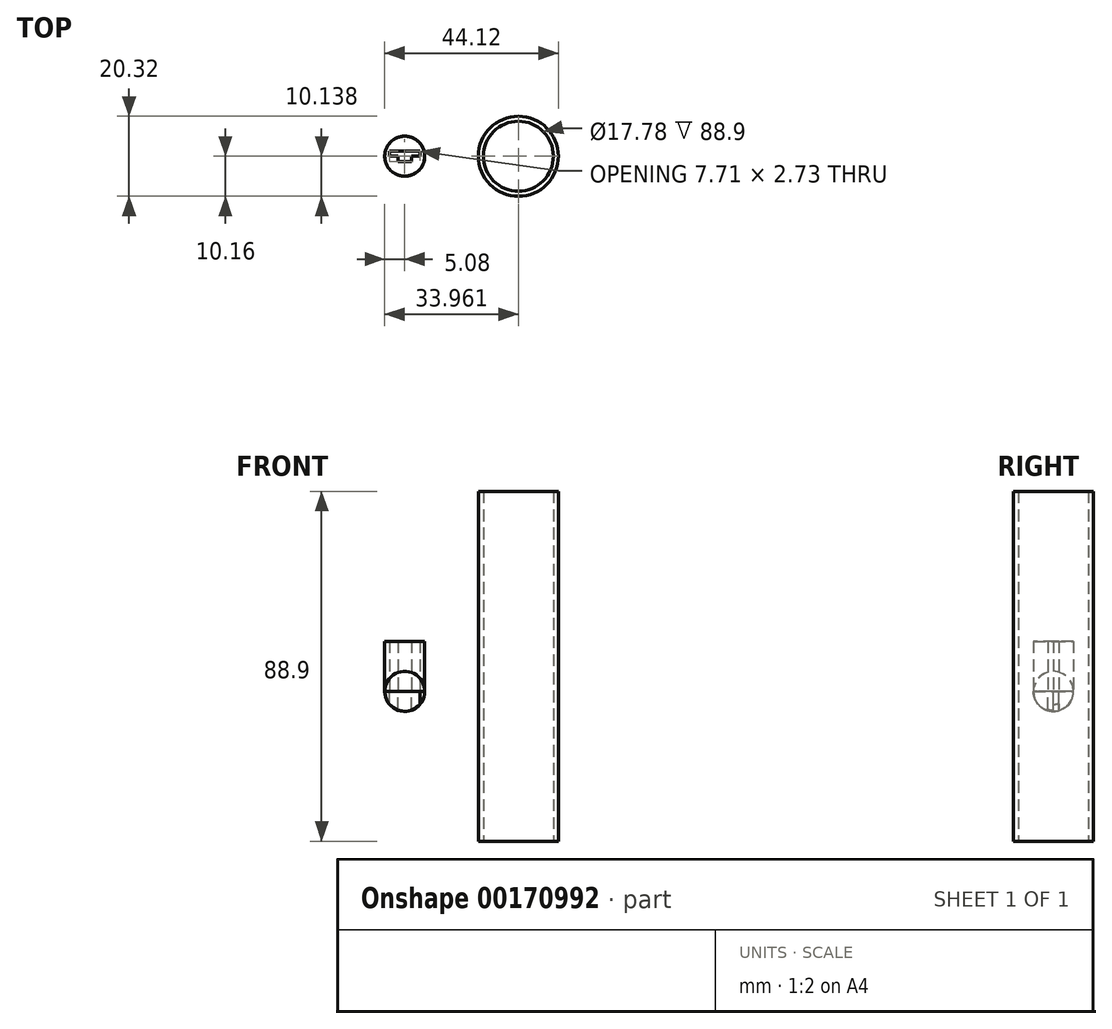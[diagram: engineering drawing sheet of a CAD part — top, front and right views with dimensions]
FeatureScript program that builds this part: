
annotation { "Feature Type Name" : "Feature", "Feature Type Description" : "" }
export const myFeature = defineFeature(function(context is Context, id is Id, definition is map)
    precondition{}
    {
        {
            var Q0;
            Q0=qCreatedBy(makeId("Top.planeOp"),FACE);
            var sketch = newSketch(context, id + "F0", { "sketchPlane" : qUnion([Q0])});
            skLineSegment(sketch, "E0", {"start": v(0, 1.35) * mm, "end": v(-3.86, 1.35) * mm});
            skLineSegment(sketch, "E1", {"start": v(-3.86, 0.01) * mm, "end": v(-1.71, 0.01) * mm});
            skLineSegment(sketch, "E2", {"start": v(-1.71, 0.01) * mm, "end": v(-1.71, -1.37) * mm});
            skLineSegment(sketch, "E3", {"start": v(-1.71, -1.37) * mm, "end": v(0, -1.37) * mm});
            skLineSegment(sketch, "E4", {"start": v(-3.86, 1.35) * mm, "end": v(-3.86, 0.01) * mm});
            skLineSegment(sketch, "E5.MirrorCS", {"start": v(1.71, 0.01) * mm, "end": v(1.71, -1.37) * mm});
            skLineSegment(sketch, "E6.MirrorCS", {"start": v(3.86, 1.35) * mm, "end": v(3.86, 0.01) * mm});
            skLineSegment(sketch, "E7.MirrorCS", {"start": v(3.86, 0.01) * mm, "end": v(1.71, 0.01) * mm});
            skLineSegment(sketch, "E8.MirrorCS", {"start": v(1.71, -1.37) * mm, "end": v(0, -1.37) * mm});
            skLineSegment(sketch, "E9.MirrorCS", {"start": v(0, 1.35) * mm, "end": v(3.86, 1.35) * mm});
            skCircle(sketch, "E10", {"center": v(0, 0) * mm, "radius": 5.08 * mm});
            skLineSegment(sketch, "E11", {"start": v(0, 0) * mm, "end": v(0, 1.35) * mm});
            skLineSegment(sketch, "E12", {"start": v(0, 0) * mm, "end": v(0, -1.37) * mm});
            skSolve(sketch);
        }
        {
            var Q0;
            Q0=makeQuery(id+"F0.imprint","IMPRINT",FACE,{"disambiguationData":[TD([[makeQuery(id+"F0.imprint","IMPRINT",EDGE,{"derivedFrom":sQuery(id+"F0.wireOp",EDGE,"E0")}),-1.0]])]});
            cPlane(context, id + "F1", {"entities" : qUnion([Q0]), "cplaneType" : CPlaneType.OFFSET, "offset" : 6.35 * mm, "width" : 152.4 * mm, "height" : 152.4 * mm});
        }
        {
            var Q0;
            Q0=makeQuery(id+"F0.imprint","IMPRINT",FACE,{"disambiguationData":[TD([[makeQuery(id+"F0.imprint","IMPRINT",EDGE,{"derivedFrom":sQuery(id+"F0.wireOp",EDGE,"E0")}),-1.0]])]});
            cPlane(context, id + "F2", {"entities" : qUnion([Q0]), "cplaneType" : CPlaneType.OFFSET, "offset" : 6.35 * mm, "oppositeDirection" : true, "width" : 152.4 * mm, "height" : 152.4 * mm});
        }
        {
            var Q0;
            Q0=qCreatedBy(id+"F1.planeOp",FACE);
            var sketch = newSketch(context, id + "F3", { "sketchPlane" : qUnion([Q0])});
            skArc(sketch, "E13", {"start": v(0, 5.08) * mm, "mid": v(-5.08, 0) * mm, "end": v(0, -5.08) * mm});
            skLineSegment(sketch, "E14", {"start": v(0, 0) * mm, "end": v(0, 1.34) * mm});
            skLineSegment(sketch, "E15", {"start": v(0, 1.34) * mm, "end": v(-3.86, 1.34) * mm});
            skLineSegment(sketch, "E16.MirrorCS", {"start": v(0, 1.34) * mm, "end": v(3.86, 1.34) * mm});
            skLineSegment(sketch, "E17", {"start": v(3.86, 1.34) * mm, "end": v(3.86, 0) * mm});
            skLineSegment(sketch, "E18", {"start": v(3.86, 0) * mm, "end": v(1.71, 0) * mm});
            skLineSegment(sketch, "E19", {"start": v(1.71, 0) * mm, "end": v(1.71, -1.39) * mm});
            skLineSegment(sketch, "E20", {"start": v(1.71, -1.39) * mm, "end": v(-1.71, -1.39) * mm});
            skLineSegment(sketch, "E21", {"start": v(-1.71, -1.39) * mm, "end": v(-1.71, 0) * mm});
            skLineSegment(sketch, "E22", {"start": v(-1.71, 0) * mm, "end": v(-3.86, 0) * mm});
            skLineSegment(sketch, "E23", {"start": v(-3.86, 0) * mm, "end": v(-3.86, 1.34) * mm});
            skLineSegment(sketch, "E24", {"start": v(-6.66, 0) * mm, "end": v(7.05, 0) * mm, "construction": true});
            skLineSegment(sketch, "E25", {"start": v(0, 5.08) * mm, "end": v(0, -5.08) * mm});
            skPoint(sketch, "E25.endSnap0", {"position": v(0, -1.39) * mm});
            skSolve(sketch);
        }
        {
            var Q0;
            Q0=qCreatedBy(id+"F2.planeOp",FACE);
            var sketch = newSketch(context, id + "F4", { "sketchPlane" : qUnion([Q0])});
            skArc(sketch, "E26", {"start": v(0, 5.08) * mm, "mid": v(-5.08, 0) * mm, "end": v(0, -5.08) * mm});
            skLineSegment(sketch, "E27", {"start": v(0, 0) * mm, "end": v(0, 1.34) * mm});
            skLineSegment(sketch, "E28", {"start": v(0, 1.34) * mm, "end": v(-3.86, 1.34) * mm});
            skLineSegment(sketch, "E29.MirrorCS", {"start": v(0, 1.34) * mm, "end": v(3.86, 1.34) * mm});
            skLineSegment(sketch, "E30", {"start": v(3.86, 1.34) * mm, "end": v(3.86, 0) * mm});
            skLineSegment(sketch, "E31", {"start": v(3.86, 0) * mm, "end": v(1.71, 0) * mm});
            skLineSegment(sketch, "E32", {"start": v(1.71, 0) * mm, "end": v(1.71, -1.39) * mm});
            skLineSegment(sketch, "E33", {"start": v(1.71, -1.39) * mm, "end": v(-1.71, -1.39) * mm});
            skLineSegment(sketch, "E34", {"start": v(-1.71, -1.39) * mm, "end": v(-1.71, 0) * mm});
            skLineSegment(sketch, "E35", {"start": v(-1.71, 0) * mm, "end": v(-3.86, 0) * mm});
            skLineSegment(sketch, "E36", {"start": v(-3.86, 0) * mm, "end": v(-3.86, 1.34) * mm});
            skLineSegment(sketch, "E37", {"start": v(-6.79, 0) * mm, "end": v(6.73, 0) * mm, "construction": true});
            skLineSegment(sketch, "E38", {"start": v(0, 5.08) * mm, "end": v(0, -5.08) * mm});
            skPoint(sketch, "E38.endSnap0", {"position": v(0, -1.39) * mm});
            skSolve(sketch);
        }
        {
            var Q0;
            {var subQ5=sQuery(id+"F3.wireOp",EDGE,"E13");Q0=makeQuery(id+"F3.imprint","IMPRINT",FACE,{"disambiguationData":[TD([[makeQuery(id+"F3.imprint","IMPRINT",EDGE,{"derivedFrom":subQ5}),1.0]])]});}
            var Q1;
            {var subQ4=sQuery(id+"F3.wireOp",EDGE,"E15");Q1=makeQuery(id+"F3.imprint","IMPRINT",FACE,{"disambiguationData":[TD([[makeQuery(id+"F3.imprint","IMPRINT",EDGE,{"derivedFrom":subQ4}),1.0]])]});}
            var Q2;
            Q2=sQuery(id+"F3.wireOp",EDGE,"E13");
            var Q3;
            Q3=sQuery(id+"F3.wireOp",EDGE,"E25");
            revolve(context, id + "F5", {"entities" : qUnion([Q0, Q1]), "surfaceEntities" : qUnion([Q2]), "axis" : qUnion([Q3]), "revolveType" : RevolveType.ONE_DIRECTION, "oppositeDirection" : true, "angle" : 180 * degree});
        }
        {
            var Q0;
            {var subQ1=sQuery(id+"F3.wireOp",EDGE,"E16.MirrorCS");Q0=makeQuery(id+"F3.imprint","IMPRINT",FACE,{"disambiguationData":[TD([[makeQuery(id+"F3.imprint","IMPRINT",EDGE,{"derivedFrom":subQ1}),-1.0]])]});}
            var Q1;
            {var subQ4=sQuery(id+"F3.wireOp",EDGE,"E15");Q1=makeQuery(id+"F3.imprint","IMPRINT",FACE,{"disambiguationData":[TD([[makeQuery(id+"F3.imprint","IMPRINT",EDGE,{"derivedFrom":subQ4}),1.0]])]});}
            var Q2;
            Q2=makeQuery(id+"F5.opRevolve","SWEPT_FACE",FACE,{"disambiguationData":[OSD([sQuery(id+"F3.wireOp",EDGE,"E13")])]});
            extrude(context, id + "F6", {"entities" : qUnion([Q0, Q1]), "operationType" : NewBodyOperationType.REMOVE, "endBound" : BoundingType.UP_TO_SURFACE, "oppositeDirection" : true, "endBoundEntityFace" : qUnion([Q2]), "depth" : 25.4 * mm});
        }
        {
            var Q0;
            {var subQ4=sQuery(id+"F3.wireOp",EDGE,"E15");Q0=makeQuery(id+"F3.imprint","IMPRINT",FACE,{"disambiguationData":[TD([[makeQuery(id+"F3.imprint","IMPRINT",EDGE,{"derivedFrom":subQ4}),1.0]])]});}
            var Q1;
            {var subQ1=sQuery(id+"F3.wireOp",EDGE,"E16.MirrorCS");Q1=makeQuery(id+"F3.imprint","IMPRINT",FACE,{"disambiguationData":[TD([[makeQuery(id+"F3.imprint","IMPRINT",EDGE,{"derivedFrom":subQ1}),-1.0]])]});}
            var Q2;
            Q2=sQuery(id+"F3.wireOp",EDGE,"E16.MirrorCS");
            var Q3;
            Q3=sQuery(id+"F3.wireOp",EDGE,"E17");
            var Q4;
            Q4=sQuery(id+"F3.wireOp",EDGE,"E18");
            var Q5;
            Q5=sQuery(id+"F3.wireOp",EDGE,"E19");
            var Q6;
            Q6=sQuery(id+"F3.wireOp",EDGE,"E20");
            var Q7;
            Q7=sQuery(id+"F3.wireOp",EDGE,"E21");
            var Q8;
            Q8=sQuery(id+"F3.wireOp",EDGE,"E22");
            var Q9;
            Q9=sQuery(id+"F3.wireOp",EDGE,"E23");
            var Q10;
            Q10=sQuery(id+"F3.wireOp",EDGE,"E15");
            var Q11;
            Q11=makeQuery(id+"F5.opRevolve","SWEPT_FACE",FACE,{"disambiguationData":[OSD([sQuery(id+"F3.wireOp",EDGE,"E13")])]});
            extrude(context, id + "F7", {"entities" : qUnion([Q0, Q1]), "operationType" : NewBodyOperationType.REMOVE, "surfaceEntities" : qUnion([Q2, Q3, Q4, Q5, Q6, Q7, Q8, Q9, Q10]), "endBound" : BoundingType.UP_TO_SURFACE, "endBoundEntityFace" : qUnion([Q11]), "depth" : 25.4 * mm});
        }
        {
            var Q0;
            {var subQ5=sQuery(id+"F4.wireOp",EDGE,"E26");Q0=makeQuery(id+"F4.imprint","IMPRINT",FACE,{"disambiguationData":[TD([[makeQuery(id+"F4.imprint","IMPRINT",EDGE,{"derivedFrom":subQ5}),1.0]])]});}
            var Q1;
            {var subQ4=sQuery(id+"F4.wireOp",EDGE,"E28");Q1=makeQuery(id+"F4.imprint","IMPRINT",FACE,{"disambiguationData":[TD([[makeQuery(id+"F4.imprint","IMPRINT",EDGE,{"derivedFrom":subQ4}),1.0]])]});}
            var Q2;
            Q2=sQuery(id+"F4.wireOp",EDGE,"E38");
            revolve(context, id + "F8", {"entities" : qUnion([Q0, Q1]), "axis" : qUnion([Q2]), "revolveType" : RevolveType.ONE_DIRECTION, "angle" : 180 * degree});
        }
        {
            var Q0;
            {var subQ1=sQuery(id+"F4.wireOp",EDGE,"E29.MirrorCS");Q0=makeQuery(id+"F4.imprint","IMPRINT",FACE,{"disambiguationData":[TD([[makeQuery(id+"F4.imprint","IMPRINT",EDGE,{"derivedFrom":subQ1}),-1.0]])]});}
            var Q1;
            {var subQ4=sQuery(id+"F4.wireOp",EDGE,"E28");Q1=makeQuery(id+"F4.imprint","IMPRINT",FACE,{"disambiguationData":[TD([[makeQuery(id+"F4.imprint","IMPRINT",EDGE,{"derivedFrom":subQ4}),1.0]])]});}
            var Q2;
            Q2=makeQuery(id+"F8.opRevolve","SWEPT_FACE",FACE,{"disambiguationData":[OSD([sQuery(id+"F4.wireOp",EDGE,"E26")])]});
            extrude(context, id + "F9", {"entities" : qUnion([Q0, Q1]), "operationType" : NewBodyOperationType.REMOVE, "endBound" : BoundingType.UP_TO_SURFACE, "oppositeDirection" : true, "endBoundEntityFace" : qUnion([Q2]), "depth" : 25.4 * mm});
        }
        {
            var Q0;
            Q0 = qSketchRegion(id + "F0", true);
            extrude(context, id + "F10", {"entities" : qUnion([Q0]), "depth" : 6.35 * mm, "hasSecondDirection" : true, "secondDirectionOppositeDirection" : true, "secondDirectionDepth" : 6.35 * mm});
        }
        {
            var Q0;
            Q0=qCreatedBy(makeId("Top.planeOp"),FACE);
            var sketch = newSketch(context, id + "F11", { "sketchPlane" : qUnion([Q0])});
            skCircle(sketch, "E39", {"center": v(28.88, 0) * mm, "radius": 8.9 * mm});
            skCircle(sketch, "E40", {"center": v(28.88, 0) * mm, "radius": 10.16 * mm});
            skSolve(sketch);
        }
        {
            var Q0;
            Q0=makeQuery(id+"F11.imprint","IMPRINT",FACE,{"disambiguationData":[TD([[makeQuery(id+"F11.imprint","IMPRINT",EDGE,{"derivedFrom":sQuery(id+"F11.wireOp",EDGE,"E39")}),-1.0]])]});
            extrude(context, id + "F12", {"entities" : qUnion([Q0]), "endBound" : BoundingType.SYMMETRIC, "depth" : 88.9 * mm});
        }
    });
